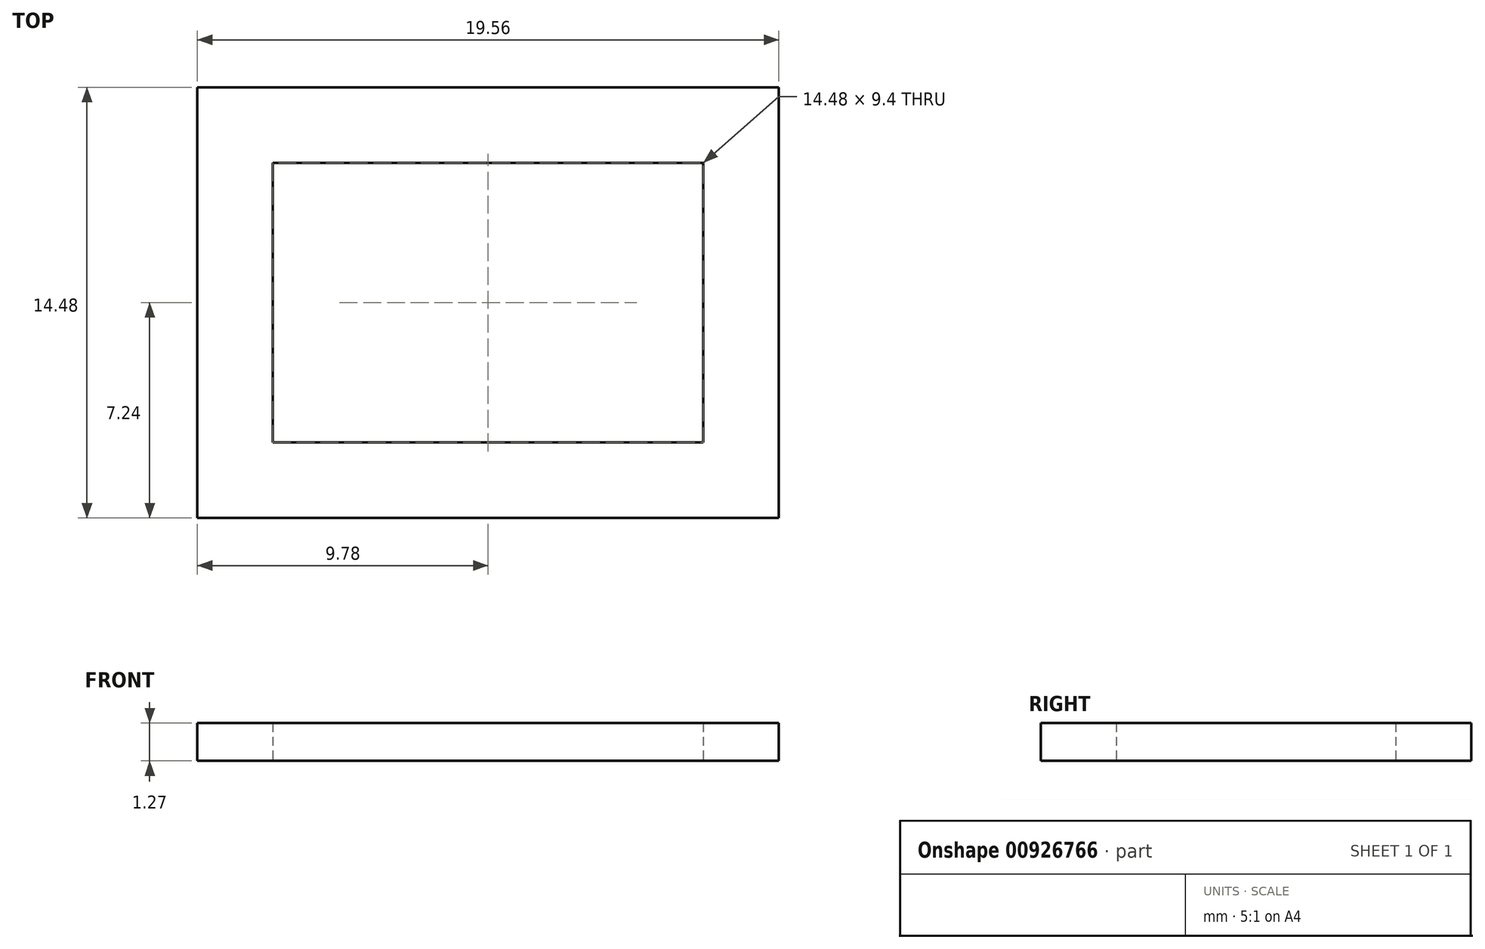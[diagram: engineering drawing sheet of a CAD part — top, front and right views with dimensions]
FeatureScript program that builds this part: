
annotation { "Feature Type Name" : "Feature", "Feature Type Description" : "" }
export const myFeature = defineFeature(function(context is Context, id is Id, definition is map)
    precondition{}
    {
        {
            var Q0;
            Q0=qCreatedBy(makeId("Top.planeOp"),FACE);
            var sketch = newSketch(context, id + "F0", { "sketchPlane" : qUnion([Q0])});
            skLineSegment(sketch, "E0.bottom", {"start": v(-7.24, 4.7) * mm, "end": v(7.24, 4.7) * mm});
            skLineSegment(sketch, "E0.top", {"start": v(-7.24, -4.7) * mm, "end": v(7.24, -4.7) * mm});
            skLineSegment(sketch, "E0.left", {"start": v(-7.24, 4.7) * mm, "end": v(-7.24, -4.7) * mm});
            skLineSegment(sketch, "E0.right", {"start": v(7.24, 4.7) * mm, "end": v(7.24, -4.7) * mm});
            skPoint(sketch, "E0.middle", {"position": v(0, 0) * mm});
            skLineSegment(sketch, "E1.bottom", {"start": v(-9.78, 7.24) * mm, "end": v(9.78, 7.24) * mm});
            skLineSegment(sketch, "E1.top", {"start": v(-9.78, -7.24) * mm, "end": v(9.78, -7.24) * mm});
            skLineSegment(sketch, "E1.left", {"start": v(-9.78, 7.24) * mm, "end": v(-9.78, -7.24) * mm});
            skLineSegment(sketch, "E1.right", {"start": v(9.78, 7.24) * mm, "end": v(9.78, -7.24) * mm});
            skSolve(sketch);
        }
        {
            var Q0;
            Q0 = qSketchRegion(id + "F0", true);
            extrude(context, id + "F1", {"entities" : qUnion([Q0]), "depth" : 1.27 * mm, "offsetDistance" : 25.4 * mm});
        }
    });
